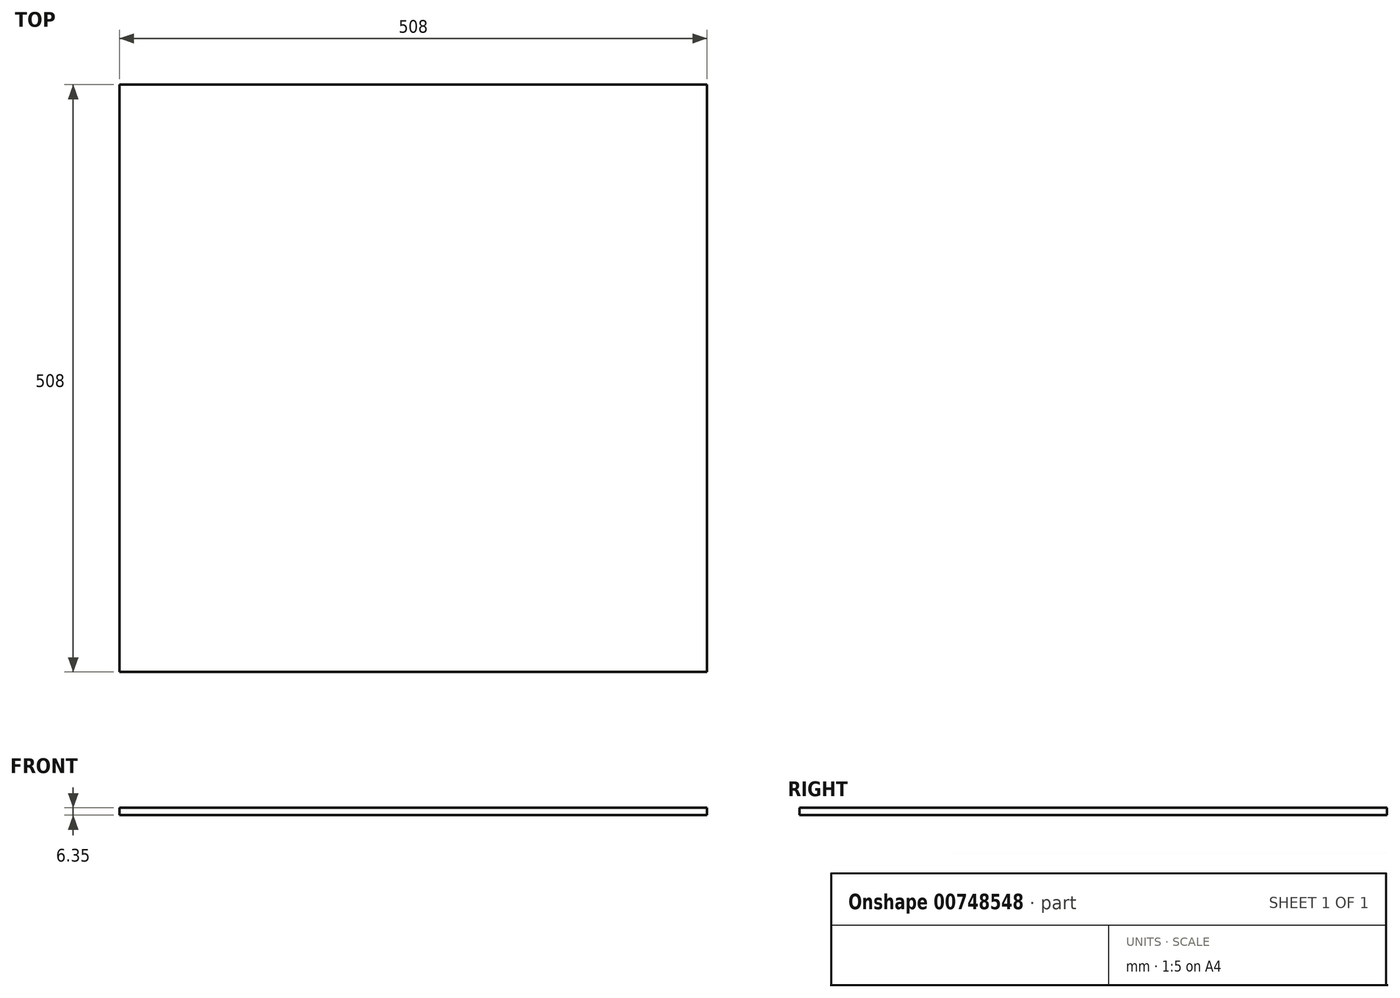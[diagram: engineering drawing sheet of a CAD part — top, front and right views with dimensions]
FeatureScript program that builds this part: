
annotation { "Feature Type Name" : "Feature", "Feature Type Description" : "" }
export const myFeature = defineFeature(function(context is Context, id is Id, definition is map)
    precondition{}
    {
        {
            var Q0;
            Q0=qCreatedBy(makeId("Top.planeOp"),FACE);
            var sketch = newSketch(context, id + "F0", { "sketchPlane" : qUnion([Q0])});
            skLineSegment(sketch, "E0.bottom", {"start": v(-272.82, -248.95) * mm, "end": v(235.18, -248.95) * mm});
            skLineSegment(sketch, "E0.top", {"start": v(-272.82, 259.05) * mm, "end": v(235.18, 259.05) * mm});
            skLineSegment(sketch, "E0.left", {"start": v(-272.82, -248.95) * mm, "end": v(-272.82, 259.05) * mm});
            skLineSegment(sketch, "E0.right", {"start": v(235.18, -248.95) * mm, "end": v(235.18, 259.05) * mm});
            skSolve(sketch);
        }
        {
            var Q0;
            Q0=qSketchRegion(id+"F0",true);
            extrude(context, id + "F1", {"entities" : qUnion([Q0]), "depth" : 6.35 * mm, "offsetDistance" : 25.4 * mm});
        }
    });
